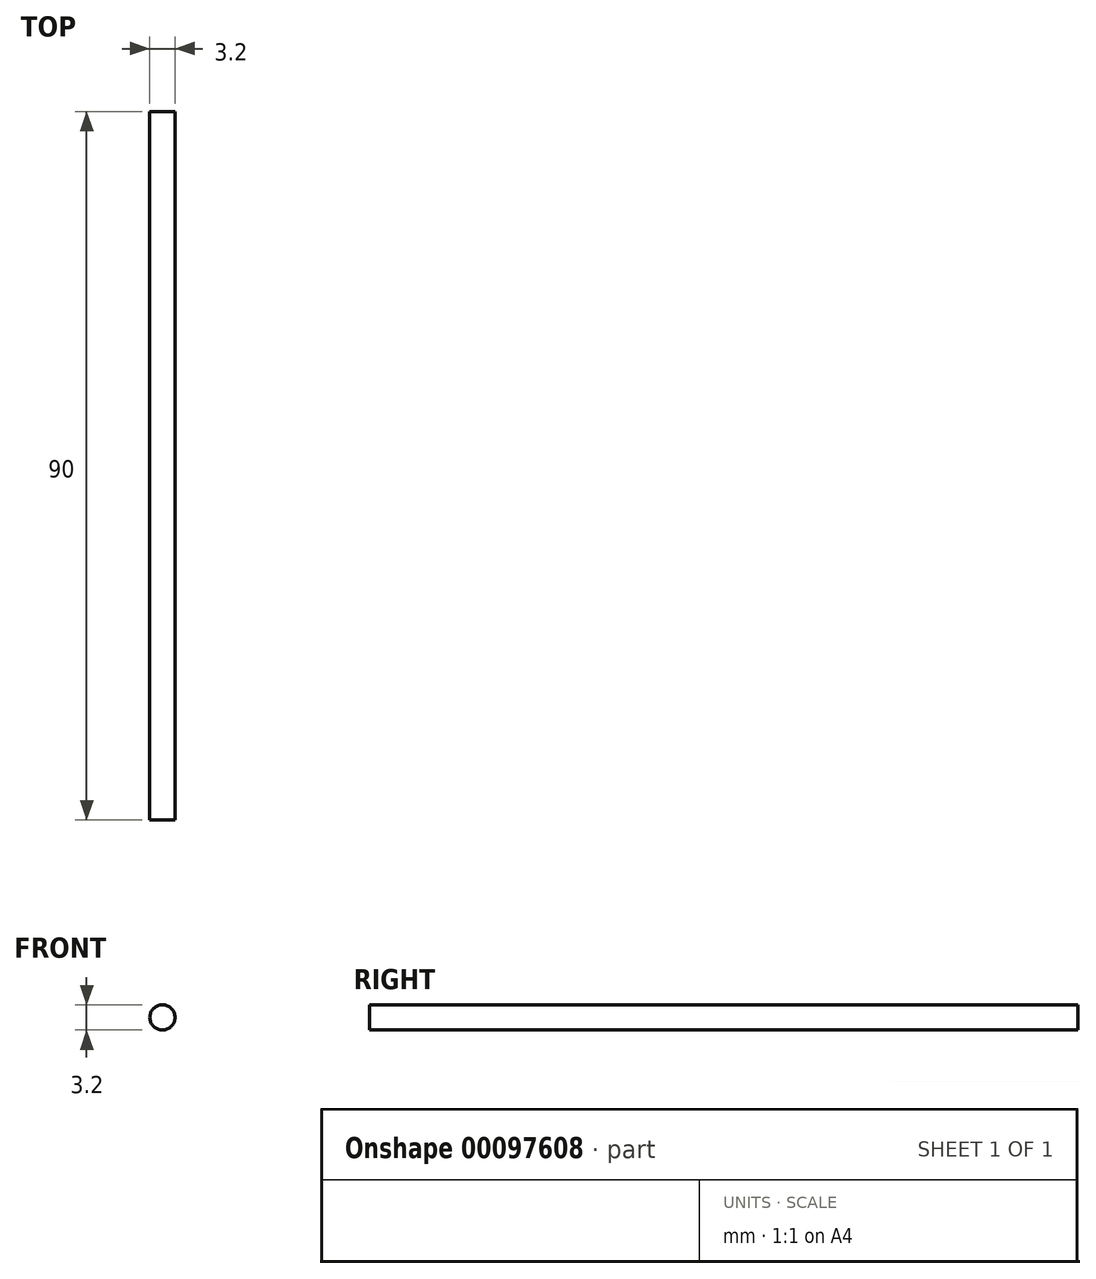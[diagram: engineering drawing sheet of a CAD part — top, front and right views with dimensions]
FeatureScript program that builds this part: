
annotation { "Feature Type Name" : "Feature", "Feature Type Description" : "" }
export const myFeature = defineFeature(function(context is Context, id is Id, definition is map)
    precondition{}
    {
        {
            var Q0;
            Q0=qCreatedBy(makeId("Front.planeOp"),FACE);
            var sketch = newSketch(context, id + "F0", { "sketchPlane" : qUnion([Q0])});
            skCircle(sketch, "E0", {"center": v(0, 0) * mm, "radius": 1.6 * mm});
            skSolve(sketch);
        }
        {
            var Q0;
            Q0 = qSketchRegion(id + "F0", true);
            extrude(context, id + "F1", {"entities" : qUnion([Q0]), "depth" : 90 * mm});
        }
    });
